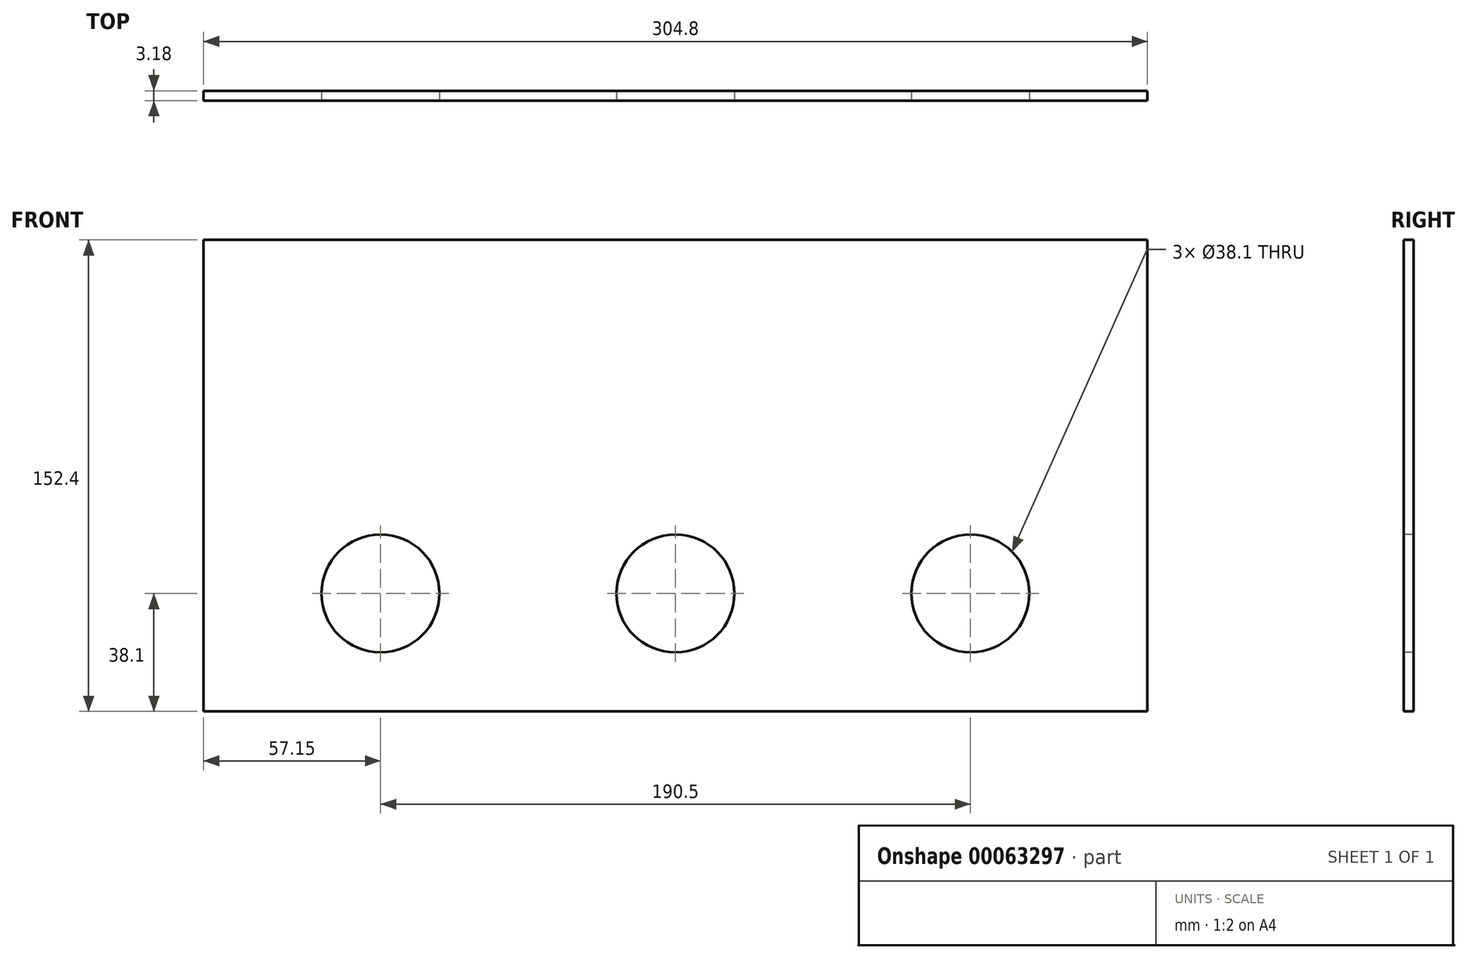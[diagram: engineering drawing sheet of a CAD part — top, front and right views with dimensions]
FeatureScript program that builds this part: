
annotation { "Feature Type Name" : "Feature", "Feature Type Description" : "" }
export const myFeature = defineFeature(function(context is Context, id is Id, definition is map)
    precondition{}
    {
        {
            var Q0;
            Q0=qCreatedBy(makeId("Front.planeOp"),FACE);
            var sketch = newSketch(context, id + "F0", { "sketchPlane" : qUnion([Q0])});
            skLineSegment(sketch, "E0.rect.bottom", {"start": v(152.4, 76.2) * mm, "end": v(-152.4, 76.2) * mm});
            skLineSegment(sketch, "E0.rect.top", {"start": v(152.4, -76.2) * mm, "end": v(-152.4, -76.2) * mm});
            skLineSegment(sketch, "E0.rect.left", {"start": v(152.4, 76.2) * mm, "end": v(152.4, -76.2) * mm});
            skLineSegment(sketch, "E0.rect.right", {"start": v(-152.4, 76.2) * mm, "end": v(-152.4, -76.2) * mm});
            skPoint(sketch, "E0.rect.middle", {"position": v(0, 0) * mm});
            skSolve(sketch);
        }
        {
            var Q0;
            Q0=makeQuery(id+"F0.imprint","IMPRINT",FACE,{"disambiguationData":[TD([[makeQuery(id+"F0.imprint","IMPRINT",EDGE,{"derivedFrom":sQuery(id+"F0.wireOp",EDGE,"E0.rect.bottom")}),1.0]])]});
            extrude(context, id + "F1", {"entities" : qUnion([Q0]), "depth" : 3.17 * mm, "symmetric" : true});
        }
        {
            var Q0;
            Q0=makeQuery(id+"F1.opExtrude","CAP_FACE",FACE,{"disambiguationData":[OSD([sQuery(id+"F0.wireOp",EDGE,"E0.rect.bottom"),sQuery(id+"F0.wireOp",EDGE,"E0.rect.top"),sQuery(id+"F0.wireOp",EDGE,"E0.rect.left"),sQuery(id+"F0.wireOp",EDGE,"E0.rect.right")])],"isStart":false});
            var sketch = newSketch(context, id + "F2", { "sketchPlane" : qUnion([Q0])});
            skCircle(sketch, "E1", {"center": v(-95.25, -38.1) * mm, "radius": 19.05 * mm});
            skCircle(sketch, "E2", {"center": v(0, -38.1) * mm, "radius": 19.05 * mm});
            skCircle(sketch, "E3", {"center": v(95.25, -38.1) * mm, "radius": 19.05 * mm});
            skPoint(sketch, "E4.endSnap0", {"position": v(0, -76.2) * mm});
            skSolve(sketch);
        }
        {
            var Q0;
            Q0 = qSketchRegion(id + "F2", true);
            extrude(context, id + "F3", {"entities" : qUnion([Q0]), "operationType" : NewBodyOperationType.REMOVE, "endBound" : BoundingType.THROUGH_ALL, "oppositeDirection" : true, "depth" : 25.4 * mm});
        }
    });
